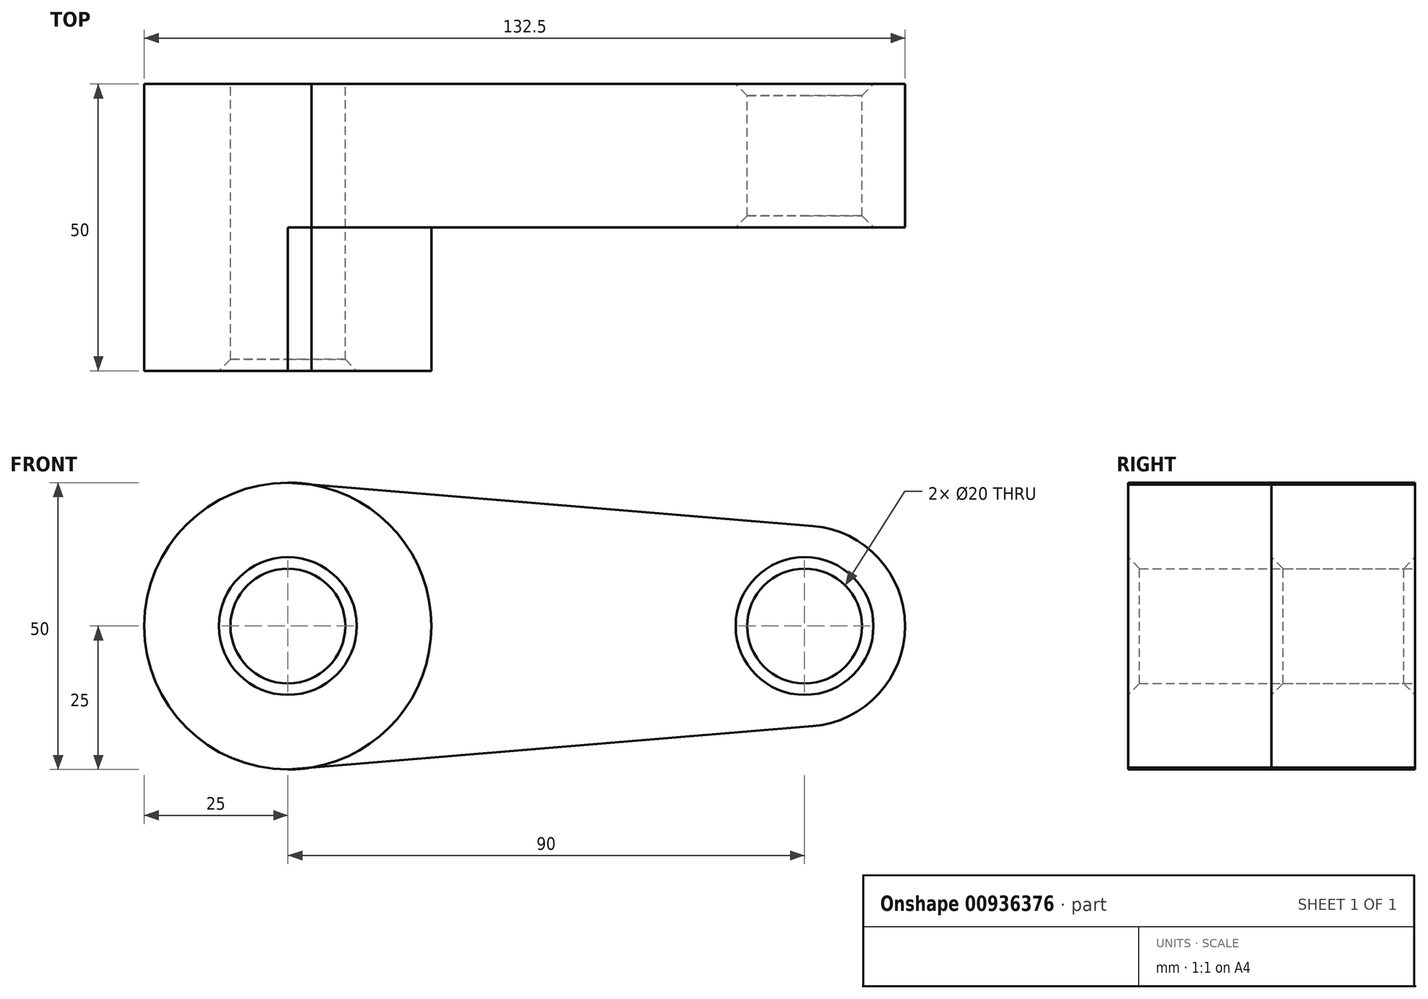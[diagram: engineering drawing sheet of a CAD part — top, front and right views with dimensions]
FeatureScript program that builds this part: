
annotation { "Feature Type Name" : "Feature", "Feature Type Description" : "" }
export const myFeature = defineFeature(function(context is Context, id is Id, definition is map)
    precondition{}
    {
        {
            var Q0;
            Q0=qCreatedBy(makeId("Front.planeOp"),FACE);
            var sketch = newSketch(context, id + "F0", { "sketchPlane" : qUnion([Q0])});
            skCircle(sketch, "E0", {"center": v(0, 0) * mm, "radius": 25 * mm});
            skCircle(sketch, "E1", {"center": v(90, 0) * mm, "radius": 17.5 * mm});
            skLineSegment(sketch, "E2", {"start": v(0, 25) * mm, "end": v(91.44, 17.44) * mm});
            skLineSegment(sketch, "E3", {"start": v(0, -25) * mm, "end": v(91.44, -17.44) * mm});
            skCircle(sketch, "E4", {"center": v(0, 0) * mm, "radius": 10 * mm});
            skCircle(sketch, "E5", {"center": v(90, 0) * mm, "radius": 10 * mm});
            skSolve(sketch);
        }
        {
            var Q0;
            Q0 = qSketchRegion(id + "F0", true);
            extrude(context, id + "F1", {"entities" : qUnion([Q0]), "depth" : 25 * mm, "offsetDistance" : 25 * mm});
        }
        {
            var Q0;
            Q0=makeQuery(id+"F0.imprint","IMPRINT",FACE,{"disambiguationData":[TD([[makeQuery(id+"F0.imprint","IMPRINT",EDGE,{"derivedFrom":sQuery(id+"F0.wireOp",EDGE,"E4")}),-1.0]])]});
            extrude(context, id + "F2", {"entities" : qUnion([Q0]), "operationType" : NewBodyOperationType.ADD, "depth" : 50 * mm, "offsetDistance" : 25 * mm});
        }
        {
            var Q0;
            {var subQ0=sQuery(id+"F0.wireOp",EDGE,"E0");Q0=makeQuery(id+"F2.opExtrude","CAP_EDGE",EDGE,{"disambiguationData":[OSD([subQ0]),TDD([makeQuery(id+"F0.imprint","IMPRINT",EDGE,{"disambiguationData":[TD([[makeQuery(id+"F0.imprint","INTERSECT",VERTEX,{"disambiguationData":[OD(1.0)],"derivedFrom":[subQ0,sQuery(id+"F0.wireOp",EDGE,"E2")]}),1.0]])],"derivedFrom":subQ0})])],"isStart":false});}
            var Q1;
            Q1=makeQuery(id+"F2.opExtrude","CAP_EDGE",EDGE,{"disambiguationData":[OSD([sQuery(id+"F0.wireOp",EDGE,"E4")])],"isStart":false});
            var Q2;
            Q2=makeQuery(id+"F1.opExtrude","CAP_EDGE",EDGE,{"disambiguationData":[OSD([sQuery(id+"F0.wireOp",EDGE,"E5")])],"isStart":true});
            var Q3;
            Q3=makeQuery(id+"F1.opExtrude","CAP_EDGE",EDGE,{"disambiguationData":[OSD([sQuery(id+"F0.wireOp",EDGE,"E5")])],"isStart":false});
            chamfer(context, id + "F3", {"entities" : qUnion([Q0, Q1, Q2, Q3]), "width" : 2 * mm, "tangentPropagation" : true});
        }
    });
